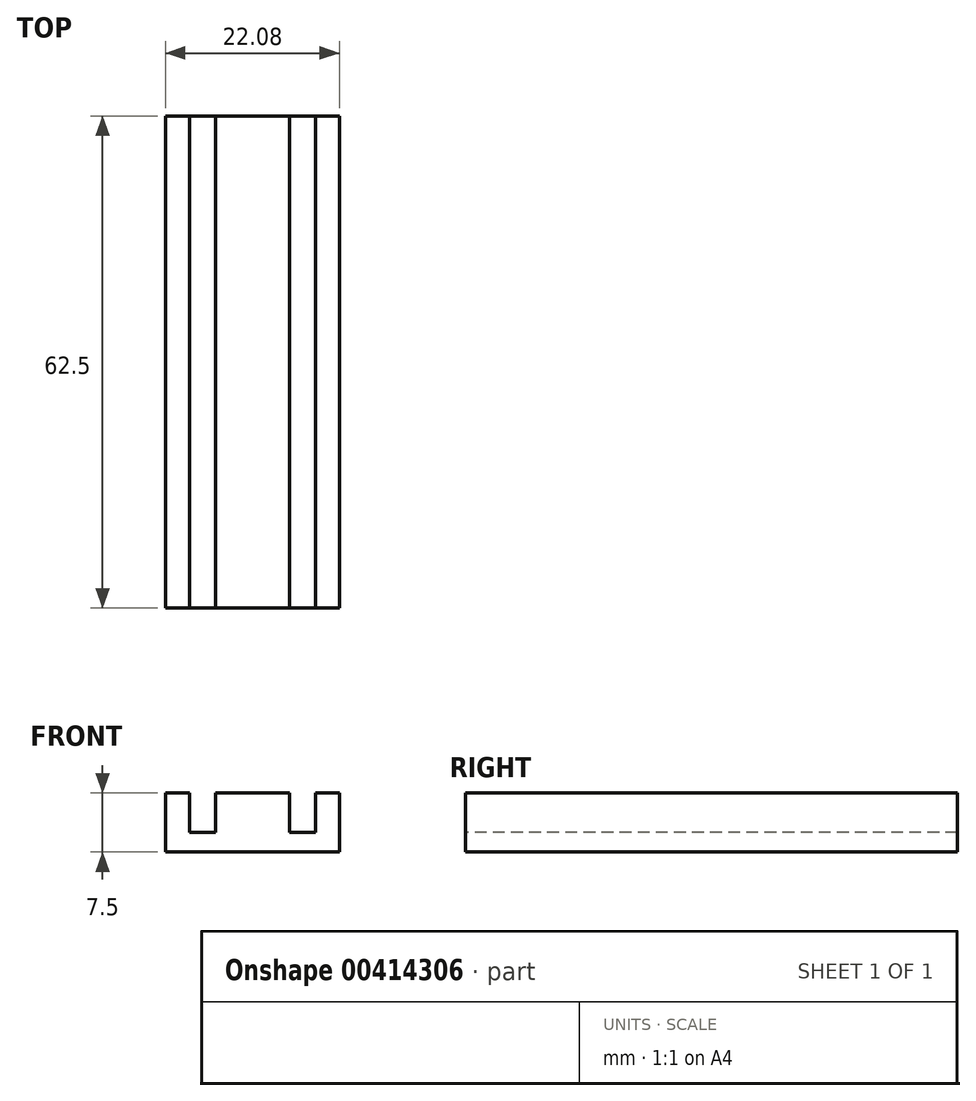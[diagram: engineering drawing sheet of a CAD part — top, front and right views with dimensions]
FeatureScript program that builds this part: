
annotation { "Feature Type Name" : "Feature", "Feature Type Description" : "" }
export const myFeature = defineFeature(function(context is Context, id is Id, definition is map)
    precondition{}
    {
        {
            var Q0;
            Q0=qCreatedBy(makeId("Top.planeOp"),FACE);
            var sketch = newSketch(context, id + "F0", { "sketchPlane" : qUnion([Q0])});
            skLineSegment(sketch, "E0.left", {"start": v(-41.9, -30.45) * mm, "end": v(-41.9, -92.95) * mm});
            skLineSegment(sketch, "E0.right", {"start": v(-38.58, -30.45) * mm, "end": v(-38.58, -92.95) * mm});
            skLineSegment(sketch, "E1.left", {"start": v(-29.2, -30.45) * mm, "end": v(-29.2, -92.95) * mm});
            skLineSegment(sketch, "E1.right", {"start": v(-25.88, -30.45) * mm, "end": v(-25.88, -92.95) * mm});
            skLineSegment(sketch, "E2", {"start": v(-22.85, -30.45) * mm, "end": v(-22.85, -92.95) * mm});
            skLineSegment(sketch, "E3", {"start": v(-44.93, -30.45) * mm, "end": v(-44.93, -92.95) * mm});
            skLineSegment(sketch, "E4", {"start": v(-22.85, -92.95) * mm, "end": v(-44.93, -92.95) * mm});
            skLineSegment(sketch, "E5", {"start": v(-22.85, -30.45) * mm, "end": v(-44.93, -30.45) * mm});
            skSolve(sketch);
        }
        {
            var Q0;
            {var subQ0=sQuery(id+"F0.wireOp",EDGE,"E0.left");Q0=makeQuery(id+"F0.imprint","IMPRINT",FACE,{"disambiguationData":[TD([[makeQuery(id+"F0.imprint","IMPRINT",EDGE,{"derivedFrom":subQ0}),-1.0]])]});}
            var Q1;
            {var subQ0=sQuery(id+"F0.wireOp",EDGE,"E0.right");Q1=makeQuery(id+"F0.imprint","IMPRINT",FACE,{"disambiguationData":[TD([[makeQuery(id+"F0.imprint","IMPRINT",EDGE,{"derivedFrom":subQ0}),1.0]])]});}
            var Q2;
            {var subQ0=sQuery(id+"F0.wireOp",EDGE,"E1.right");Q2=makeQuery(id+"F0.imprint","IMPRINT",FACE,{"disambiguationData":[TD([[makeQuery(id+"F0.imprint","IMPRINT",EDGE,{"derivedFrom":subQ0}),1.0]])]});}
            extrude(context, id + "F1", {"entities" : qUnion([Q0, Q1, Q2]), "depth" : 5 * mm});
        }
        {
            var Q0;
            Q0 = qSketchRegion(id + "F0", true);
            extrude(context, id + "F2", {"entities" : qUnion([Q0]), "operationType" : NewBodyOperationType.ADD, "oppositeDirection" : true, "depth" : 2.5 * mm});
        }
    });
